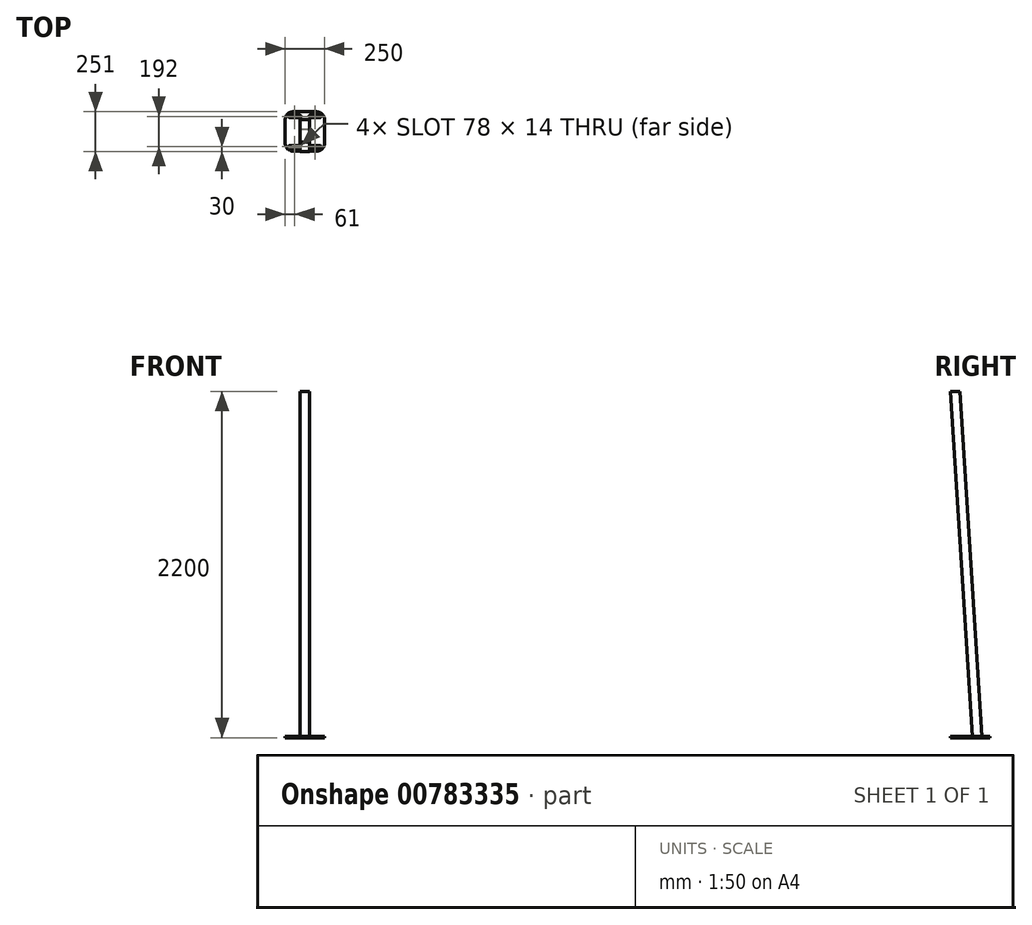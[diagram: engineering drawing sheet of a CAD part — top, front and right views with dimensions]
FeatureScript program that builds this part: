
annotation { "Feature Type Name" : "Feature", "Feature Type Description" : "" }
export const myFeature = defineFeature(function(context is Context, id is Id, definition is map)
    precondition{}
    {
        {
            var Q0;
            Q0=qCreatedBy(makeId("Top.planeOp"),FACE);
            var sketch = newSketch(context, id + "F0", { "sketchPlane" : qUnion([Q0])});
            skLineSegment(sketch, "E0.bottom", {"start": v(-50, 0) * mm, "end": v(-200, 0) * mm});
            skLineSegment(sketch, "E0.top", {"start": v(-50, 250) * mm, "end": v(-200, 250) * mm});
            skLineSegment(sketch, "E0.left", {"start": v(0, 50) * mm, "end": v(0, 200) * mm});
            skLineSegment(sketch, "E0.right", {"start": v(-250, 50) * mm, "end": v(-250, 200) * mm});
            skPoint(sketch, "E1.visualSharp", {"position": v(-250, 0) * mm});
            skArc(sketch, "E1.filletArc", {"start": v(-250, 50) * mm, "mid": v(-235.36, 14.64) * mm, "end": v(-200, 0) * mm});
            skPoint(sketch, "E2.visualSharp", {"position": v(-250, 250) * mm});
            skArc(sketch, "E2.filletArc", {"start": v(-200, 250) * mm, "mid": v(-235.36, 235.36) * mm, "end": v(-250, 200) * mm});
            skPoint(sketch, "E3.visualSharp", {"position": v(0, 250) * mm});
            skArc(sketch, "E3.filletArc", {"start": v(0, 200) * mm, "mid": v(-14.64, 235.36) * mm, "end": v(-50, 250) * mm});
            skPoint(sketch, "E4.visualSharp", {"position": v(0, 0) * mm});
            skArc(sketch, "E4.filletArc", {"start": v(-50, 0) * mm, "mid": v(-14.64, 14.64) * mm, "end": v(0, 50) * mm});
            skLineSegment(sketch, "E5", {"start": v(-221, 36) * mm, "end": v(-157, 36) * mm});
            skArc(sketch, "E6", {"start": v(-157, 22) * mm, "mid": v(-150, 29) * mm, "end": v(-157, 36) * mm});
            skArc(sketch, "E7", {"start": v(-221, 36) * mm, "mid": v(-228, 29) * mm, "end": v(-221, 22) * mm});
            skLineSegment(sketch, "E8", {"start": v(-221, 22) * mm, "end": v(-157, 22) * mm});
            skLineSegment(sketch, "E9", {"start": v(-125, 0) * mm, "end": v(-125, 250) * mm, "construction": true});
            skLineSegment(sketch, "E10.MirrorCS", {"start": v(-29, 36) * mm, "end": v(-93, 36) * mm});
            skLineSegment(sketch, "E11.MirrorCS", {"start": v(-29, 22) * mm, "end": v(-93, 22) * mm});
            skArc(sketch, "E12.MirrorCS", {"start": v(-93, 22) * mm, "mid": v(-100, 29) * mm, "end": v(-93, 36) * mm});
            skArc(sketch, "E13.MirrorCS", {"start": v(-29, 36) * mm, "mid": v(-22, 29) * mm, "end": v(-29, 22) * mm});
            skLineSegment(sketch, "E14", {"start": v(-250, 125) * mm, "end": v(0, 125) * mm, "construction": true});
            skLineSegment(sketch, "E15.MirrorCS", {"start": v(-221, 214) * mm, "end": v(-157, 214) * mm});
            skLineSegment(sketch, "E16.MirrorCS", {"start": v(-221, 228) * mm, "end": v(-157, 228) * mm});
            skArc(sketch, "E17.MirrorCS", {"start": v(-221, 214) * mm, "mid": v(-228, 221) * mm, "end": v(-221, 228) * mm});
            skArc(sketch, "E18.MirrorCS", {"start": v(-157, 228) * mm, "mid": v(-150, 221) * mm, "end": v(-157, 214) * mm});
            skArc(sketch, "E19.MirrorCS", {"start": v(-93, 228) * mm, "mid": v(-100, 221) * mm, "end": v(-93, 214) * mm});
            skLineSegment(sketch, "E20.MirrorCS", {"start": v(-29, 214) * mm, "end": v(-93, 214) * mm});
            skArc(sketch, "E21.MirrorCS", {"start": v(-29, 214) * mm, "mid": v(-22, 221) * mm, "end": v(-29, 228) * mm});
            skLineSegment(sketch, "E22.MirrorCS", {"start": v(-29, 228) * mm, "end": v(-93, 228) * mm});
            skSolve(sketch);
        }
        {
            var Q0;
            Q0 = qSketchRegion(id + "F0", true);
            extrude(context, id + "F1", {"entities" : qUnion([Q0]), "depth" : 10 * mm, "offsetDistance" : 25 * mm});
        }
        {
            var Q0;
            Q0=makeQuery(id+"F1.opExtrude","CAP_FACE",FACE,{"disambiguationData":[OSD([sQuery(id+"F0.wireOp",EDGE,"E0.bottom"),sQuery(id+"F0.wireOp",EDGE,"E0.top"),sQuery(id+"F0.wireOp",EDGE,"E0.left"),sQuery(id+"F0.wireOp",EDGE,"E0.right"),sQuery(id+"F0.wireOp",EDGE,"E1.filletArc"),sQuery(id+"F0.wireOp",EDGE,"E2.filletArc"),sQuery(id+"F0.wireOp",EDGE,"E3.filletArc"),sQuery(id+"F0.wireOp",EDGE,"E4.filletArc")])],"isStart":false});
            var sketch = newSketch(context, id + "F2", { "sketchPlane" : qUnion([Q0])});
            skLineSegment(sketch, "E23.bottom", {"start": v(-155, 140) * mm, "end": v(-95, 140) * mm});
            skLineSegment(sketch, "E23.top", {"start": v(-155, 200) * mm, "end": v(-95, 200) * mm});
            skLineSegment(sketch, "E23.left", {"start": v(-155, 140) * mm, "end": v(-155, 200) * mm});
            skLineSegment(sketch, "E23.right", {"start": v(-95, 140) * mm, "end": v(-95, 200) * mm});
            skLineSegment(sketch, "E24", {"start": v(-125, 140) * mm, "end": v(-125, 0) * mm, "construction": true});
            skLineSegment(sketch, "E25", {"start": v(-125, 200) * mm, "end": v(-125, 250) * mm, "construction": true});
            skSolve(sketch);
        }
        {
            var Q0;
            Q0=qCreatedBy(makeId("Right.planeOp"),FACE);
            var sketch = newSketch(context, id + "F3", { "sketchPlane" : qUnion([Q0])});
            skLineSegment(sketch, "E26", {"start": v(29, 2200) * mm, "end": v(170, 10) * mm});
            skLineSegment(sketch, "E27", {"start": v(29, 2200) * mm, "end": v(29, 0) * mm, "construction": true});
            skSolve(sketch);
        }
        {
            var Q0;
            Q0 = qSketchRegion(id + "F2", true);
            var Q1;
            Q1 = qConstructionFilter(qBodyType(qCreatedBy(id + "F3" ,EDGE), BodyType.WIRE), ConstructionObject.NO);
            sweep(context, id + "F4", {"operationType" : NewBodyOperationType.ADD, "profiles" : qUnion([Q0]), "path" : qUnion([Q1])});
        }
    });
